# Revit family: Sanitary_Other-Sanitary_AXOR_39201XXX-AXOR-Citterio-Single-lever-bide_
name_source: partatom
category: Plumbing Fixtures
revit_build: Autodesk Revit 2018 (Build: 20170223_1515(x64)
units: mm (PartAtom-declared; Revit-internal decimal feet)

## family parameters
Always vertical = No
Cut with Voids When Loaded = No
OmniClass Number = 23.40.20.00
OmniClass Title = General Furniture and Specialties
Part Type = Normal
Room Calculation Point = No
Round Connector Dimension = Use Diameter
Shared = No
Work Plane-Based = No

## types (1)
- Default - please load Revit Family Type Catalog
    Always visible = Yes
    BIMobject category = Other Sanitary
    Design country = Germany
    EAN code = 4059625358726
    Edition number = 1
    GTIN code = https://4059625358726
    IFC Classification = Sanitary Terminal
    Installation instructions = https://www.axor-design.com
    Manufacturer country = Germany
    Manufacturer name = AXOR
    Material 1 = AXOR - AXOR Citterio - 000 Chrome
    Material main = Chrome
    Product Guid = bdbd2cb6-2431-4c7b-af53-9b8357976708
    Product SKU = 39201XXX
    Product data url = https://www.bimobject.com
    Product family = AXOR Citterio
    Product group = Bidet mixers
    Product name = 39201XXX AXOR Citterio Single lever bidet mixer with lever handle and pop-up waste set - rhombic cut
    Product url = https://www.axor-design.com
    QR code = https://www.bimobject.com
    Technical description = https://www.axor-design.com

## geometry (parser evidence)
native form markers: Sweep x1
no freeform markers — native parametric forms only
